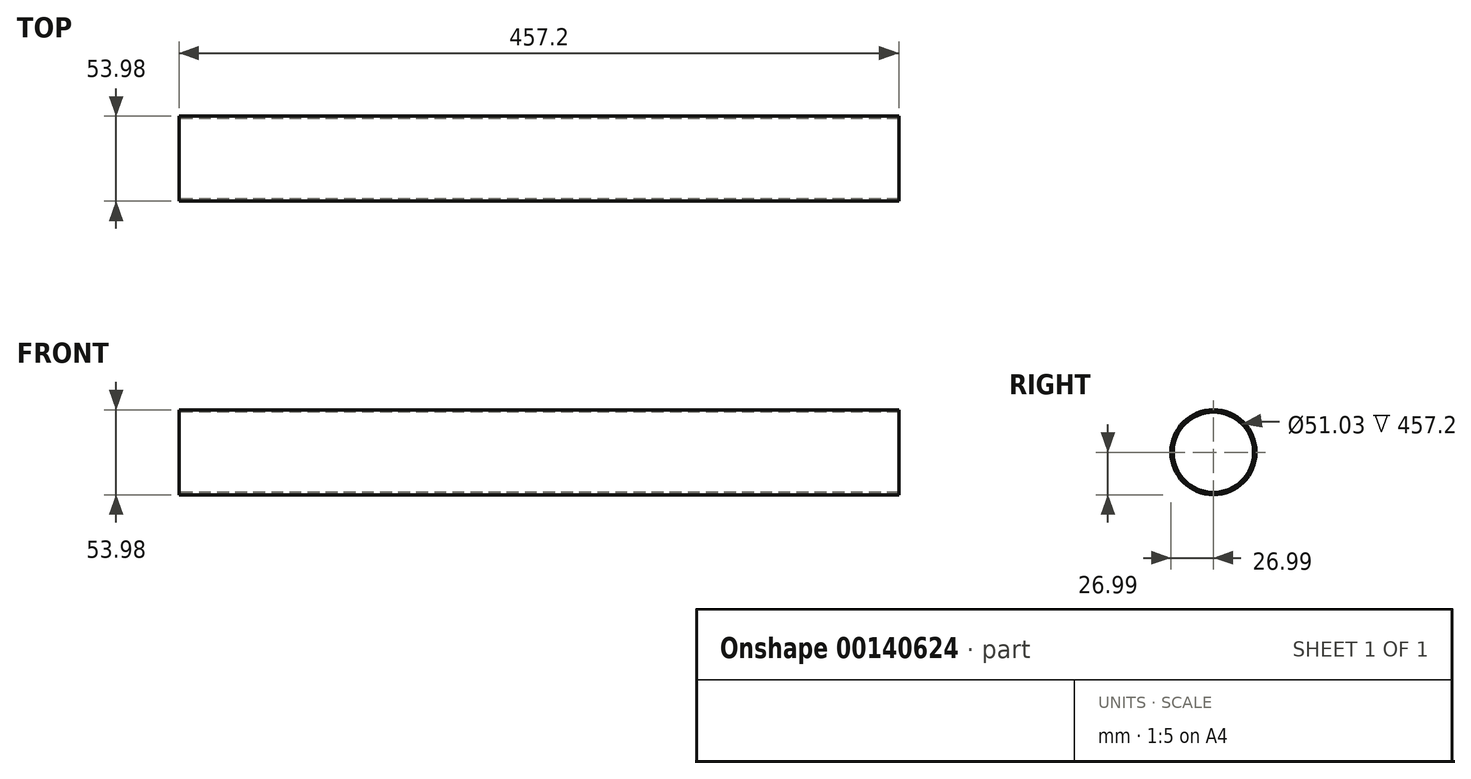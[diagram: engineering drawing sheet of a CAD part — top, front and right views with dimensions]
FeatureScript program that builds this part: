
annotation { "Feature Type Name" : "Feature", "Feature Type Description" : "" }
export const myFeature = defineFeature(function(context is Context, id is Id, definition is map)
    precondition{}
    {
        {
            var Q0;
            Q0=qCreatedBy(makeId("Right.planeOp"),FACE);
            var sketch = newSketch(context, id + "F0", { "sketchPlane" : qUnion([Q0])});
            skCircle(sketch, "E0", {"center": v(0, 0) * mm, "radius": 25.51 * mm});
            skCircle(sketch, "E1.0", {"center": v(0, 0) * mm, "radius": 26.99 * mm});
            skSolve(sketch);
        }
        {
            var Q0;
            Q0=makeQuery(id+"F0.imprint","IMPRINT",FACE,{"disambiguationData":[TD([[makeQuery(id+"F0.imprint","IMPRINT",EDGE,{"derivedFrom":sQuery(id+"F0.wireOp",EDGE,"E0")}),-1.0]])]});
            extrude(context, id + "F1", {"entities" : qUnion([Q0]), "depth" : 457.2 * mm});
        }
    });
